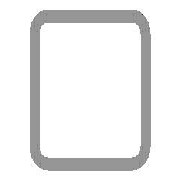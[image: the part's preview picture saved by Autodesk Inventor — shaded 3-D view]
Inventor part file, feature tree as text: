
AUTODESK INVENTOR PART (.ipt)
format: ipt  version: 2025.1 (Build 291241020, 241B)  size: 136,704 bytes
history: native  units: mm (DEFAULTED — no unit token found)
features: other x4, sketch x1, plane x1
ambient origin geometry x8: Origin, YZ Plane, XZ Plane, XY Plane, X Axis, Y Axis, Z Axis, Center Point
bodies: Solid1 (feature_tree), Body (feature_tree)
feature tree (6):
  parser-record x1  (decoder bookkeeping rows leaked as tree rows — omitted from the tree; the rows remain in map.json)
  other  "Driven Length"
  other  "Start plane"
  other  "End plane"
  sketch  "Sketch3"  dims[d3=550.0mm d4=0.0mm d7=6.0mm d9=100.0mm d11=100.0mm d12=3.0mm d13=100.0mm d14=650.0mm d15=50.0mm d16=50.0mm d17=90.0deg d18=550.0mm]
  plane  "Work Plane3"
